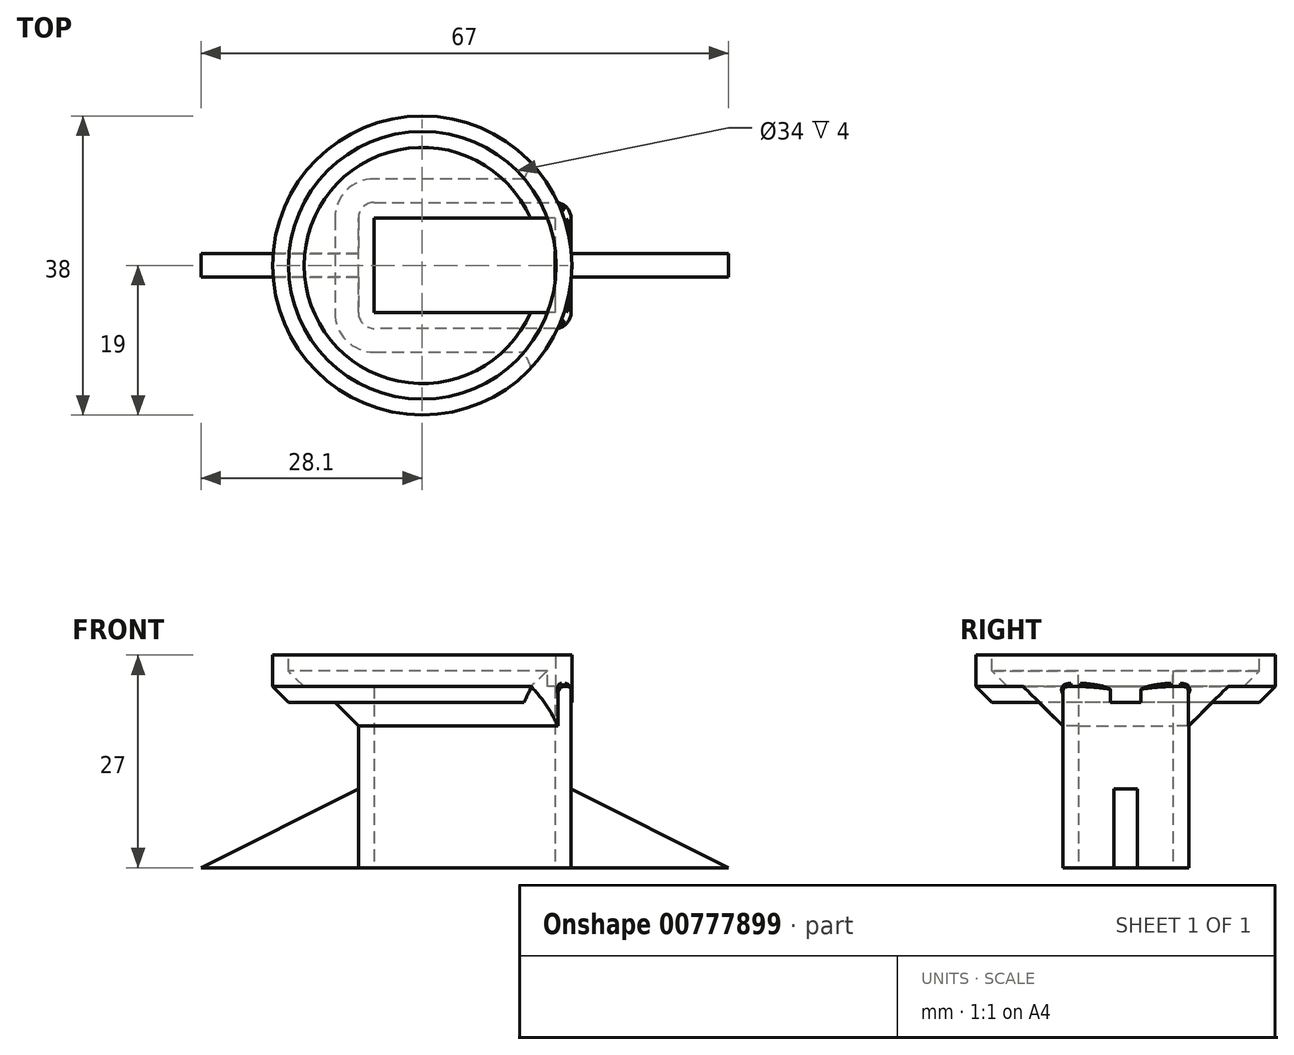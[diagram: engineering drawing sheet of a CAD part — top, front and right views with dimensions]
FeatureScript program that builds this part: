
annotation { "Feature Type Name" : "Feature", "Feature Type Description" : "" }
export const myFeature = defineFeature(function(context is Context, id is Id, definition is map)
    precondition{}
    {
        {
            var Q0;
            Q0=qCreatedBy(makeId("Top.planeOp"),FACE);
            var sketch = newSketch(context, id + "F0", { "sketchPlane" : qUnion([Q0])});
            skLineSegment(sketch, "E0.bottom", {"start": v(11.5, 6) * mm, "end": v(-11.5, 6) * mm});
            skLineSegment(sketch, "E0.top", {"start": v(11.5, -6) * mm, "end": v(-11.5, -6) * mm});
            skLineSegment(sketch, "E0.left", {"start": v(11.5, 6) * mm, "end": v(11.5, -6) * mm});
            skLineSegment(sketch, "E0.right", {"start": v(-11.5, 6) * mm, "end": v(-11.5, -6) * mm});
            skPoint(sketch, "E0.middle", {"position": v(0, 0) * mm});
            skLineSegment(sketch, "E1.0", {"start": v(-13.5, 8) * mm, "end": v(-13.5, -8) * mm});
            skLineSegment(sketch, "E1.1", {"start": v(13.5, 8) * mm, "end": v(-13.5, 8) * mm});
            skLineSegment(sketch, "E1.2", {"start": v(13.5, 8) * mm, "end": v(13.5, -8) * mm});
            skLineSegment(sketch, "E1.3", {"start": v(13.5, -8) * mm, "end": v(-13.5, -8) * mm});
            skSolve(sketch);
        }
        {
            var Q0;
            Q0=makeQuery(id+"F0.imprint","IMPRINT",FACE,{"disambiguationData":[TD([[makeQuery(id+"F0.imprint","IMPRINT",EDGE,{"derivedFrom":sQuery(id+"F0.wireOp",EDGE,"E0.bottom")}),-1.0]])]});
            extrude(context, id + "F1", {"entities" : qUnion([Q0]), "depth" : 23 * mm, "offsetDistance" : 25 * mm});
        }
        {
            var Q0;
            Q0=makeQuery(id+"F1.opExtrude","SWEPT_EDGE",EDGE,{"disambiguationData":[OSD([sQuery(id+"F0.wireOp",EDGE,"E1.0"),sQuery(id+"F0.wireOp",EDGE,"E1.1")])]});
            var Q1;
            Q1=makeQuery(id+"F1.opExtrude","SWEPT_EDGE",EDGE,{"disambiguationData":[OSD([sQuery(id+"F0.wireOp",EDGE,"E1.2"),sQuery(id+"F0.wireOp",EDGE,"E1.3")])]});
            var Q2;
            Q2=makeQuery(id+"F1.opExtrude","SWEPT_EDGE",EDGE,{"disambiguationData":[OSD([sQuery(id+"F0.wireOp",EDGE,"E1.0"),sQuery(id+"F0.wireOp",EDGE,"E1.3")])]});
            var Q3;
            Q3=makeQuery(id+"F1.opExtrude","SWEPT_EDGE",EDGE,{"disambiguationData":[OSD([sQuery(id+"F0.wireOp",EDGE,"E1.1"),sQuery(id+"F0.wireOp",EDGE,"E1.2")])]});
            fillet(context, id + "F2", {"entities" : qUnion([Q0, Q1, Q2, Q3]), "radius" : 2 * mm, "tangentPropagation" : true, "allowEdgeOverflow" : false});
        }
        {
            var Q0;
            Q0=qCreatedBy(makeId("Front.planeOp"),FACE);
            var sketch = newSketch(context, id + "F3", { "sketchPlane" : qUnion([Q0])});
            skLineSegment(sketch, "E2.0", {"start": v(13.5, 10) * mm, "end": v(13.5, 0) * mm});
            skLineSegment(sketch, "E3", {"start": v(13.5, 10) * mm, "end": v(33.5, 0) * mm});
            skLineSegment(sketch, "E4", {"start": v(33.5, 0) * mm, "end": v(13.5, 0) * mm});
            skSolve(sketch);
        }
        {
            var Q0;
            Q0=makeQuery(id+"F3.imprint","IMPRINT",FACE,{"disambiguationData":[TD([[makeQuery(id+"F3.imprint","IMPRINT",EDGE,{"derivedFrom":sQuery(id+"F3.wireOp",EDGE,"E2.0")}),1.0]])]});
            extrude(context, id + "F4", {"entities" : qUnion([Q0]), "operationType" : NewBodyOperationType.ADD, "endBound" : BoundingType.SYMMETRIC, "depth" : 3 * mm, "offsetDistance" : 25 * mm});
        }
        {
            var Q0;
            Q0=makeQuery(id+"F1.opExtrude","SWEPT_BODY",BODY,{"disambiguationData":[OSD([sQuery(id+"F0.wireOp",EDGE,"E0.bottom"),sQuery(id+"F0.wireOp",EDGE,"E0.top"),sQuery(id+"F0.wireOp",EDGE,"E0.left"),sQuery(id+"F0.wireOp",EDGE,"E0.right"),sQuery(id+"F0.wireOp",EDGE,"E1.0"),sQuery(id+"F0.wireOp",EDGE,"E1.1"),sQuery(id+"F0.wireOp",EDGE,"E1.2"),sQuery(id+"F0.wireOp",EDGE,"E1.3")])]});
            var Q1;
            Q1=qCreatedBy(makeId("Right.planeOp"),FACE);
            mirror(context, id + "F5", {"operationType" : NewBodyOperationType.ADD, "entities" : qUnion([Q0]), "mirrorPlane" : qUnion([Q1])});
        }
        {
            var Q0;
            Q0=qCreatedBy(makeId("Top.planeOp"),FACE);
            cPlane(context, id + "F6", {"entities" : qUnion([Q0]), "cplaneType" : CPlaneType.OFFSET, "offset" : 27 * mm, "width" : 150 * mm, "height" : 150 * mm});
        }
        {
            var Q0;
            Q0=qCreatedBy(id+"F6.planeOp",FACE);
            var sketch = newSketch(context, id + "F7", { "sketchPlane" : qUnion([Q0])});
            skCircle(sketch, "E5", {"center": v(-5.4, 0) * mm, "radius": 17 * mm});
            skCircle(sketch, "E6.0", {"center": v(-5.4, 0) * mm, "radius": 19 * mm});
            skSolve(sketch);
        }
        {
            var Q0;
            Q0=makeQuery(id+"F7.imprint","IMPRINT",FACE,{"disambiguationData":[TD([[makeQuery(id+"F7.imprint","IMPRINT",EDGE,{"derivedFrom":sQuery(id+"F7.wireOp",EDGE,"E5")}),-1.0]])]});
            extrude(context, id + "F8", {"entities" : qUnion([Q0]), "oppositeDirection" : true, "depth" : 6 * mm, "offsetDistance" : 25 * mm});
        }
        {
            var Q0;
            Q0=makeQuery(id+"F1.opExtrude","SWEPT_BODY",BODY,{"disambiguationData":[OSD([sQuery(id+"F0.wireOp",EDGE,"E0.bottom"),sQuery(id+"F0.wireOp",EDGE,"E0.top"),sQuery(id+"F0.wireOp",EDGE,"E0.left"),sQuery(id+"F0.wireOp",EDGE,"E0.right"),sQuery(id+"F0.wireOp",EDGE,"E1.0"),sQuery(id+"F0.wireOp",EDGE,"E1.1"),sQuery(id+"F0.wireOp",EDGE,"E1.2"),sQuery(id+"F0.wireOp",EDGE,"E1.3")])]});
            var Q1;
            Q1=makeQuery(id+"F8.opExtrude","SWEPT_BODY",BODY,{"disambiguationData":[OSD([sQuery(id+"F7.wireOp",EDGE,"E5"),sQuery(id+"F7.wireOp",EDGE,"E6.0")])]});
            booleanBodies(context, id + "F9", {"operationType" : BooleanOperationType.UNION, "tools" : qUnion([Q0, Q1])});
        }
        {
            var Q0;
            {var subQ1=sQuery(id+"F0.wireOp",EDGE,"E1.1");var subQ3=sQuery(id+"F7.wireOp",EDGE,"E5");var subQ4=sQuery(id+"F7.wireOp",EDGE,"E6.0");Q0=makeQuery(id+"F9.opBoolean","SPLIT",FACE,{"disambiguationData":[TD([makeQuery(id+"F1.opExtrude","SWEPT_FACE",FACE,{"disambiguationData":[OSD([subQ1])]})])],"derivedFrom":makeQuery(id+"F8.opExtrude","CAP_FACE",FACE,{"disambiguationData":[OSD([subQ3,subQ4])],"isStart":false})});}
            var sketch = newSketch(context, id + "F10", { "sketchPlane" : qUnion([Q0])});
            skCircle(sketch, "E7.0", {"center": v(-5.4, 0) * mm, "radius": 19 * mm});
            skSolve(sketch);
        }
        {
            var Q0;
            Q0 = qSketchRegion(id + "F10", true);
            extrude(context, id + "F11", {"entities" : qUnion([Q0]), "operationType" : NewBodyOperationType.ADD, "oppositeDirection" : true, "depth" : 2 * mm, "offsetDistance" : 25 * mm});
        }
        {
            var Q0;
            Q0=makeQuery(id+"F11.boolean.opBoolean","INTERSECT",EDGE,{"derivedFrom":[makeQuery(id+"F1.opExtrude","SWEPT_FACE",FACE,{"disambiguationData":[OSD([sQuery(id+"F0.wireOp",EDGE,"E1.3")])]}),makeQuery(id+"F11.opExtrude","CAP_FACE",FACE,{"disambiguationData":[OSD([sQuery(id+"F10.wireOp",EDGE,"E7.0")])],"isStart":true})]});
            var Q1;
            Q1=makeQuery(id+"F11.boolean.opBoolean","INTERSECT",EDGE,{"derivedFrom":[makeQuery(id+"F2.opFillet","BLEND_FACE",FACE,{"disambiguationData":[OSD([sQuery(id+"F0.wireOp",EDGE,"E1.0"),sQuery(id+"F0.wireOp",EDGE,"E1.3")])]}),makeQuery(id+"F11.opExtrude","CAP_FACE",FACE,{"disambiguationData":[OSD([sQuery(id+"F10.wireOp",EDGE,"E7.0")])],"isStart":true})]});
            var Q2;
            Q2=makeQuery(id+"F11.boolean.opBoolean","INTERSECT",EDGE,{"derivedFrom":[makeQuery(id+"F1.opExtrude","SWEPT_FACE",FACE,{"disambiguationData":[OSD([sQuery(id+"F0.wireOp",EDGE,"E1.0")])]}),makeQuery(id+"F11.opExtrude","CAP_FACE",FACE,{"disambiguationData":[OSD([sQuery(id+"F10.wireOp",EDGE,"E7.0")])],"isStart":true})]});
            var Q3;
            Q3=makeQuery(id+"F11.boolean.opBoolean","INTERSECT",EDGE,{"derivedFrom":[makeQuery(id+"F1.opExtrude","SWEPT_FACE",FACE,{"disambiguationData":[OSD([sQuery(id+"F0.wireOp",EDGE,"E1.1")])]}),makeQuery(id+"F11.opExtrude","CAP_FACE",FACE,{"disambiguationData":[OSD([sQuery(id+"F10.wireOp",EDGE,"E7.0")])],"isStart":true})]});
            var Q4;
            Q4=makeQuery(id+"F11.boolean.opBoolean","INTERSECT",EDGE,{"derivedFrom":[makeQuery(id+"F2.opFillet","BLEND_FACE",FACE,{"disambiguationData":[OSD([sQuery(id+"F0.wireOp",EDGE,"E1.0"),sQuery(id+"F0.wireOp",EDGE,"E1.1")])]}),makeQuery(id+"F11.opExtrude","CAP_FACE",FACE,{"disambiguationData":[OSD([sQuery(id+"F10.wireOp",EDGE,"E7.0")])],"isStart":true})]});
            chamfer(context, id + "F12", {"entities" : qUnion([Q0, Q1, Q2, Q3, Q4]), "width" : 3 * mm, "tangentPropagation" : true});
        }
        {
            var Q0;
            {var subQ1=sQuery(id+"F7.wireOp",EDGE,"E5");var subQ3=makeQuery(id+"F8.opExtrude","CAP_FACE",FACE,{"disambiguationData":[OSD([subQ1,sQuery(id+"F7.wireOp",EDGE,"E6.0")])],"isStart":false});Q0=makeQuery(id+"F11.boolean.opBoolean","MERGE",FACE,{"derivedFrom":[makeQuery(id+"F9.opBoolean","SPLIT",FACE,{"disambiguationData":[TD([makeQuery(id+"F1.opExtrude","SWEPT_FACE",FACE,{"disambiguationData":[OSD([sQuery(id+"F0.wireOp",EDGE,"E0.bottom")])]})])],"derivedFrom":subQ3}),makeQuery(id+"F9.opBoolean","SPLIT",FACE,{"disambiguationData":[TD([makeQuery(id+"F1.opExtrude","SWEPT_FACE",FACE,{"disambiguationData":[OSD([sQuery(id+"F0.wireOp",EDGE,"E0.top")])]})])],"derivedFrom":subQ3}),makeQuery(id+"F11.opExtrude","CAP_FACE",FACE,{"disambiguationData":[OSD([sQuery(id+"F10.wireOp",EDGE,"E7.0")])],"isStart":true})]});}
            extrude(context, id + "F13", {"entities" : qUnion([Q0]), "operationType" : NewBodyOperationType.REMOVE, "oppositeDirection" : true, "depth" : 2 * mm, "offsetDistance" : 25 * mm});
        }
        {
            var Q0;
            Q0=makeQuery(id+"F9.opBoolean","INTERSECT",EDGE,{"disambiguationData":[OD(0.0)],"derivedFrom":[makeQuery(id+"F1.opExtrude","CAP_FACE",FACE,{"disambiguationData":[OSD([sQuery(id+"F0.wireOp",EDGE,"E0.bottom"),sQuery(id+"F0.wireOp",EDGE,"E0.top"),sQuery(id+"F0.wireOp",EDGE,"E0.left"),sQuery(id+"F0.wireOp",EDGE,"E0.right"),sQuery(id+"F0.wireOp",EDGE,"E1.0"),sQuery(id+"F0.wireOp",EDGE,"E1.1"),sQuery(id+"F0.wireOp",EDGE,"E1.2"),sQuery(id+"F0.wireOp",EDGE,"E1.3")])],"isStart":false}),makeQuery(id+"F8.opExtrude","SWEPT_FACE",FACE,{"disambiguationData":[OSD([sQuery(id+"F7.wireOp",EDGE,"E6.0")])]})]});
            var Q1;
            Q1=makeQuery(id+"F9.opBoolean","INTERSECT",EDGE,{"disambiguationData":[OD(1.0)],"derivedFrom":[makeQuery(id+"F1.opExtrude","CAP_FACE",FACE,{"disambiguationData":[OSD([sQuery(id+"F0.wireOp",EDGE,"E0.bottom"),sQuery(id+"F0.wireOp",EDGE,"E0.top"),sQuery(id+"F0.wireOp",EDGE,"E0.left"),sQuery(id+"F0.wireOp",EDGE,"E0.right"),sQuery(id+"F0.wireOp",EDGE,"E1.0"),sQuery(id+"F0.wireOp",EDGE,"E1.1"),sQuery(id+"F0.wireOp",EDGE,"E1.2"),sQuery(id+"F0.wireOp",EDGE,"E1.3")])],"isStart":false}),makeQuery(id+"F8.opExtrude","SWEPT_FACE",FACE,{"disambiguationData":[OSD([sQuery(id+"F7.wireOp",EDGE,"E6.0")])]})]});
            var Q2;
            {var subQ0=sQuery(id+"F0.wireOp",EDGE,"E1.3");var subQ1=sQuery(id+"F0.wireOp",EDGE,"E1.2");Q2=makeQuery(id+"F2.opFillet","BLEND_EDGE",EDGE,{"blendedFrom":[makeQuery(id+"F1.opExtrude","SWEPT_EDGE",EDGE,{"disambiguationData":[OSD([subQ1,subQ0])]}),makeQuery(id+"F1.opExtrude","CAP_FACE",FACE,{"disambiguationData":[OSD([sQuery(id+"F0.wireOp",EDGE,"E0.bottom"),sQuery(id+"F0.wireOp",EDGE,"E0.top"),sQuery(id+"F0.wireOp",EDGE,"E0.left"),sQuery(id+"F0.wireOp",EDGE,"E0.right"),sQuery(id+"F0.wireOp",EDGE,"E1.0"),sQuery(id+"F0.wireOp",EDGE,"E1.1"),subQ1,subQ0])],"isStart":false})],"blendedInto":[makeQuery(id+"F1.opExtrude","CAP_FACE",FACE,{"disambiguationData":[OSD([sQuery(id+"F0.wireOp",EDGE,"E0.bottom"),sQuery(id+"F0.wireOp",EDGE,"E0.top"),sQuery(id+"F0.wireOp",EDGE,"E0.left"),sQuery(id+"F0.wireOp",EDGE,"E0.right"),sQuery(id+"F0.wireOp",EDGE,"E1.0"),sQuery(id+"F0.wireOp",EDGE,"E1.1"),subQ1,subQ0])],"isStart":false})]});}
            var Q3;
            {var subQ0=sQuery(id+"F0.wireOp",EDGE,"E1.3");var subQ1=sQuery(id+"F0.wireOp",EDGE,"E1.2");Q3=makeQuery(id+"F9.opBoolean","SPLIT",EDGE,{"disambiguationData":[TD([makeQuery(id+"F2.opFillet","BLEND_FACE",FACE,{"disambiguationData":[OSD([subQ1,subQ0])]})])],"derivedFrom":makeQuery(id+"F1.opExtrude","CAP_EDGE",EDGE,{"disambiguationData":[OSD([subQ1])],"isStart":false})});}
            var Q4;
            {var subQ0=sQuery(id+"F0.wireOp",EDGE,"E1.2");var subQ1=sQuery(id+"F0.wireOp",EDGE,"E1.1");Q4=makeQuery(id+"F9.opBoolean","SPLIT",EDGE,{"disambiguationData":[TD([makeQuery(id+"F2.opFillet","BLEND_FACE",FACE,{"disambiguationData":[OSD([subQ1,subQ0])]})])],"derivedFrom":makeQuery(id+"F1.opExtrude","CAP_EDGE",EDGE,{"disambiguationData":[OSD([subQ0])],"isStart":false})});}
            var Q5;
            {var subQ0=sQuery(id+"F0.wireOp",EDGE,"E1.2");var subQ1=sQuery(id+"F0.wireOp",EDGE,"E1.1");Q5=makeQuery(id+"F2.opFillet","BLEND_EDGE",EDGE,{"blendedFrom":[makeQuery(id+"F1.opExtrude","SWEPT_EDGE",EDGE,{"disambiguationData":[OSD([subQ1,subQ0])]}),makeQuery(id+"F1.opExtrude","CAP_FACE",FACE,{"disambiguationData":[OSD([sQuery(id+"F0.wireOp",EDGE,"E0.bottom"),sQuery(id+"F0.wireOp",EDGE,"E0.top"),sQuery(id+"F0.wireOp",EDGE,"E0.left"),sQuery(id+"F0.wireOp",EDGE,"E0.right"),sQuery(id+"F0.wireOp",EDGE,"E1.0"),subQ1,subQ0,sQuery(id+"F0.wireOp",EDGE,"E1.3")])],"isStart":false})],"blendedInto":[makeQuery(id+"F1.opExtrude","CAP_FACE",FACE,{"disambiguationData":[OSD([sQuery(id+"F0.wireOp",EDGE,"E0.bottom"),sQuery(id+"F0.wireOp",EDGE,"E0.top"),sQuery(id+"F0.wireOp",EDGE,"E0.left"),sQuery(id+"F0.wireOp",EDGE,"E0.right"),sQuery(id+"F0.wireOp",EDGE,"E1.0"),subQ1,subQ0,sQuery(id+"F0.wireOp",EDGE,"E1.3")])],"isStart":false})]});}
            fillet(context, id + "F14", {"entities" : qUnion([Q0, Q1, Q2, Q3, Q4, Q5]), "radius" : 0.4 * mm, "tangentPropagation" : true, "allowEdgeOverflow" : false});
        }
        {
            var Q0;
            {var subQ0=sQuery(id+"F7.wireOp",EDGE,"E5");var subQ1=makeQuery(id+"F8.opExtrude","SWEPT_FACE",FACE,{"disambiguationData":[OSD([subQ0])]});var subQ2=sQuery(id+"F0.wireOp",EDGE,"E0.bottom");var subQ3=sQuery(id+"F10.wireOp",EDGE,"E7.0");var subQ4=sQuery(id+"F0.wireOp",EDGE,"E0.top");var subQ5=makeQuery(id+"F1.opExtrude","CAP_FACE",FACE,{"disambiguationData":[OSD([subQ2,subQ4,sQuery(id+"F0.wireOp",EDGE,"E0.left"),sQuery(id+"F0.wireOp",EDGE,"E0.right"),sQuery(id+"F0.wireOp",EDGE,"E1.0"),sQuery(id+"F0.wireOp",EDGE,"E1.1"),sQuery(id+"F0.wireOp",EDGE,"E1.2"),sQuery(id+"F0.wireOp",EDGE,"E1.3")])],"isStart":false});var subQ6=makeQuery(id+"F11.opExtrude","CAP_FACE",FACE,{"disambiguationData":[OSD([subQ3])],"isStart":false});var subQ7=subQ5;Q0=makeQuery(id+"F13.boolean.opBoolean","SPLIT",EDGE,{"disambiguationData":[topologyDisambiguationEdgeConnected([subQ5,subQ1,subQ6]),TD([makeQuery(id+"F1.opExtrude","SWEPT_FACE",FACE,{"disambiguationData":[OSD([subQ2])]})])],"derivedFrom":makeQuery(id+"F11.boolean.opBoolean","MERGE",EDGE,{"derivedFrom":[makeQuery(id+"F9.opBoolean","INTERSECT",EDGE,{"disambiguationData":[OD(0.0)],"derivedFrom":[subQ7,subQ1]}),makeQuery(id+"F9.opBoolean","INTERSECT",EDGE,{"disambiguationData":[OD(1.0)],"derivedFrom":[subQ7,subQ1]}),makeQuery(id+"F9.opBoolean","INTERSECT",EDGE,{"disambiguationData":[OD(2.0)],"derivedFrom":[subQ7,subQ1]})]})});}
            var Q1;
            {var subQ0=sQuery(id+"F0.wireOp",EDGE,"E1.2");var subQ1=sQuery(id+"F7.wireOp",EDGE,"E6.0");Q1=makeQuery(id+"F9.opBoolean","SPLIT",EDGE,{"disambiguationData":[TD([makeQuery(id+"F2.opFillet","BLEND_FACE",FACE,{"disambiguationData":[OSD([sQuery(id+"F0.wireOp",EDGE,"E1.1"),subQ0])]})])],"derivedFrom":makeQuery(id+"F8.opExtrude","CAP_EDGE",EDGE,{"disambiguationData":[OSD([subQ1])],"isStart":false})});}
            chamfer(context, id + "F15", {"entities" : qUnion([Q0, Q1]), "width" : 2 * mm, "tangentPropagation" : true});
        }
    });
